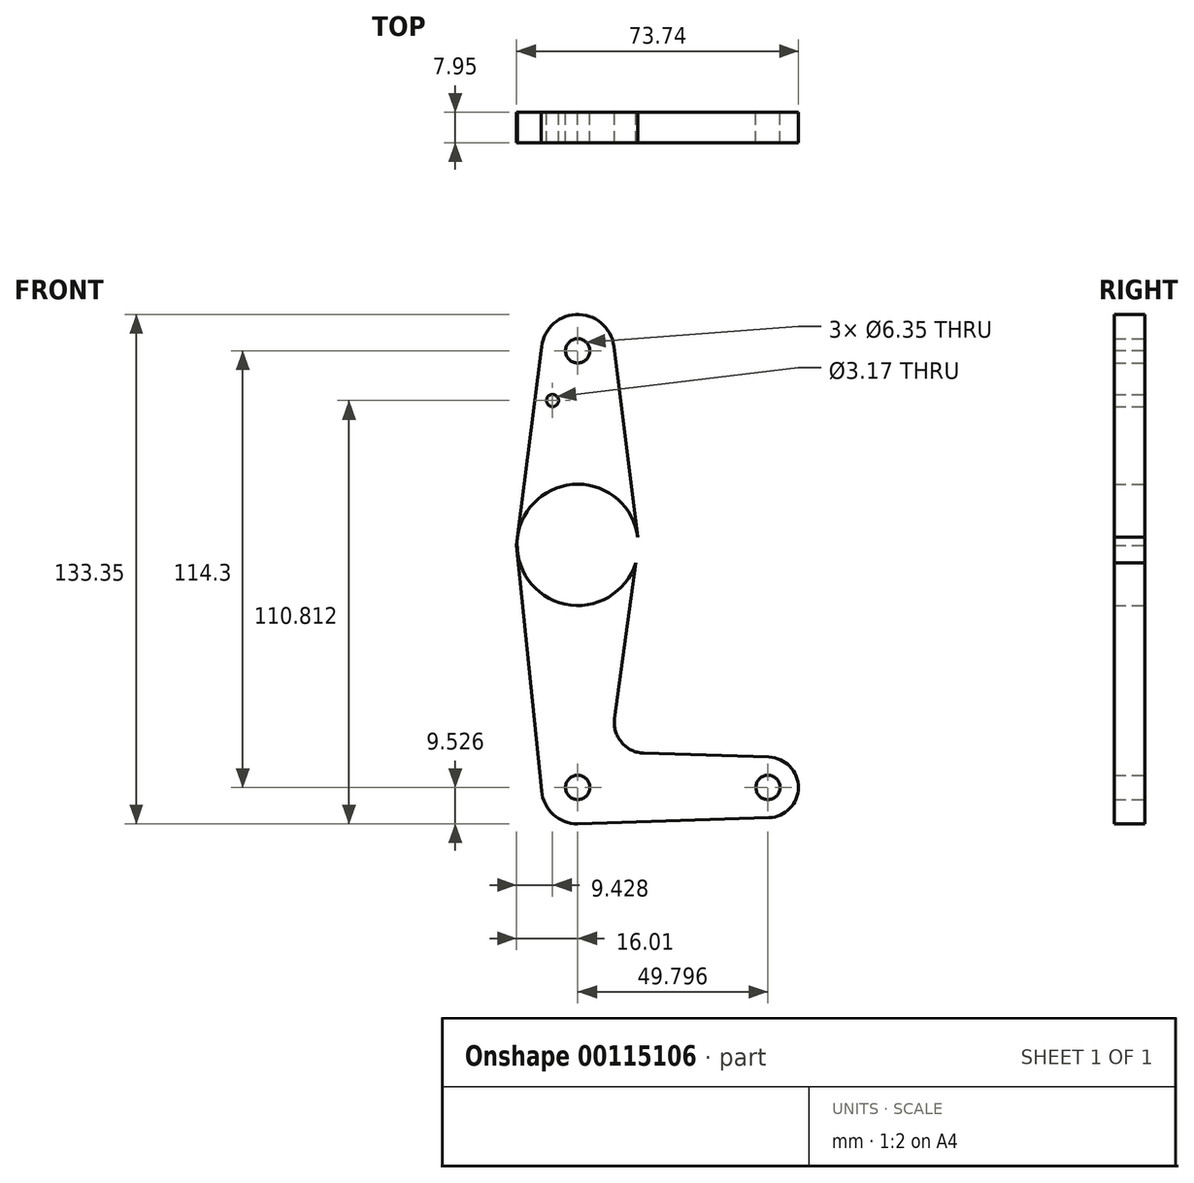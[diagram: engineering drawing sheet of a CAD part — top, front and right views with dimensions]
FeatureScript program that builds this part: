
annotation { "Feature Type Name" : "Feature", "Feature Type Description" : "" }
export const myFeature = defineFeature(function(context is Context, id is Id, definition is map)
    precondition{}
    {
        {
            var Q0;
            Q0=qCreatedBy(makeId("Front.planeOp"),FACE);
            var sketch = newSketch(context, id + "F0", { "sketchPlane" : qUnion([Q0])});
            skLineSegment(sketch, "E0", {"start": v(0, 46.97) * mm, "end": v(0, -67.33) * mm});
            skLineSegment(sketch, "E1", {"start": v(0, -67.33) * mm, "end": v(49.8, -67.33) * mm});
            skCircle(sketch, "E2", {"center": v(0, 46.97) * mm, "radius": 9.53 * mm});
            skCircle(sketch, "E3", {"center": v(0, -3.83) * mm, "radius": 15.88 * mm});
            skCircle(sketch, "E4", {"center": v(0, -67.33) * mm, "radius": 9.53 * mm});
            skCircle(sketch, "E5", {"center": v(49.8, -67.33) * mm, "radius": 7.94 * mm});
            skLineSegment(sketch, "E6", {"start": v(-9.52, 47.1) * mm, "end": v(-16.01, -3.92) * mm});
            skLineSegment(sketch, "E7", {"start": v(17.29, -58.36) * mm, "end": v(50.05, -59.4) * mm});
            skLineSegment(sketch, "E8", {"start": v(-16.01, -3.92) * mm, "end": v(-9.48, -68.3) * mm});
            skLineSegment(sketch, "E9", {"start": v(0, -76.86) * mm, "end": v(50.05, -75.27) * mm});
            skLineSegment(sketch, "E10", {"start": v(15.18, -8.49) * mm, "end": v(9.66, -49.35) * mm});
            skLineSegment(sketch, "E11", {"start": v(9.45, 48.16) * mm, "end": v(15.75, -1.85) * mm});
            skCircle(sketch, "E12", {"center": v(0, 46.97) * mm, "radius": 3.18 * mm});
            skCircle(sketch, "E13", {"center": v(0, -67.33) * mm, "radius": 3.18 * mm});
            skCircle(sketch, "E14", {"center": v(49.8, -67.33) * mm, "radius": 3.18 * mm});
            skCircle(sketch, "E15", {"center": v(0, 0) * mm, "radius": 3.18 * mm});
            skArc(sketch, "E16.filletArc", {"start": v(9.66, -49.35) * mm, "mid": v(11.47, -55.55) * mm, "end": v(17.29, -58.36) * mm});
            skCircle(sketch, "E17", {"center": v(-6.58, 33.95) * mm, "radius": 1.59 * mm});
            skSolve(sketch);
        }
        {
            var Q0;
            Q0=makeQuery(id+"F0.imprint","IMPRINT",FACE,{"disambiguationData":[TD([[makeQuery(id+"F0.imprint","IMPRINT",EDGE,{"derivedFrom":sQuery(id+"F0.wireOp",EDGE,"E17")}),-1.0]])]});
            var Q1;
            {var subQ5=sQuery(id+"F0.wireOp",EDGE,"E11");Q1=makeQuery(id+"F0.imprint","IMPRINT",FACE,{"disambiguationData":[TD([[makeQuery(id+"F0.imprint","IMPRINT",EDGE,{"derivedFrom":subQ5}),-1.0]])]});}
            var Q2;
            Q2=makeQuery(id+"F0.imprint","IMPRINT",FACE,{"disambiguationData":[TD([[makeQuery(id+"F0.imprint","IMPRINT",EDGE,{"derivedFrom":sQuery(id+"F0.wireOp",EDGE,"E12")}),-1.0]])]});
            var Q3;
            {var subQ0=sQuery(id+"F0.wireOp",EDGE,"E3");var subQ2=sQuery(id+"F0.wireOp",EDGE,"E0");var subQ3=makeQuery(id+"F0.imprint","INTERSECT",VERTEX,{"disambiguationData":[OD(0.0)],"derivedFrom":[subQ2,subQ0]});Q3=makeQuery(id+"F0.imprint","IMPRINT",FACE,{"disambiguationData":[TD([[makeQuery(id+"F0.imprint","IMPRINT",EDGE,{"disambiguationData":[TD([[subQ3,-1.0]])],"derivedFrom":subQ2}),1.0]])]});}
            var Q4;
            {var subQ0=sQuery(id+"F0.wireOp",EDGE,"E3");var subQ2=sQuery(id+"F0.wireOp",EDGE,"E0");var subQ4=makeQuery(id+"F0.imprint","INTERSECT",VERTEX,{"disambiguationData":[OD(0.0)],"derivedFrom":[subQ2,subQ0]});Q4=makeQuery(id+"F0.imprint","IMPRINT",FACE,{"disambiguationData":[TD([[makeQuery(id+"F0.imprint","IMPRINT",EDGE,{"disambiguationData":[TD([[subQ4,-1.0]])],"derivedFrom":subQ2}),-1.0]])]});}
            var Q5;
            {var subQ0=sQuery(id+"F0.wireOp",EDGE,"E8");Q5=makeQuery(id+"F0.imprint","IMPRINT",FACE,{"disambiguationData":[TD([[makeQuery(id+"F0.imprint","IMPRINT",EDGE,{"derivedFrom":subQ0}),1.0]])]});}
            var Q6;
            {var subQ10=sQuery(id+"F0.wireOp",EDGE,"E7");Q6=makeQuery(id+"F0.imprint","IMPRINT",FACE,{"disambiguationData":[TD([[makeQuery(id+"F0.imprint","IMPRINT",EDGE,{"derivedFrom":subQ10}),-1.0]])]});}
            var Q7;
            {var subQ0=sQuery(id+"F0.wireOp",EDGE,"E5");var subQ1=sQuery(id+"F0.wireOp",EDGE,"E1");var subQ2=makeQuery(id+"F0.imprint","INTERSECT",VERTEX,{"derivedFrom":[subQ1,subQ0]});Q7=makeQuery(id+"F0.imprint","IMPRINT",FACE,{"disambiguationData":[TD([[makeQuery(id+"F0.imprint","IMPRINT",EDGE,{"disambiguationData":[TD([[subQ2,1.0]])],"derivedFrom":subQ1}),-1.0]])]});}
            var Q8;
            {var subQ3=sQuery(id+"F0.wireOp",EDGE,"E4");var subQ8=sQuery(id+"F0.wireOp",EDGE,"E0");var subQ9=makeQuery(id+"F0.imprint","INTERSECT",VERTEX,{"derivedFrom":[subQ8,subQ3]});Q8=makeQuery(id+"F0.imprint","IMPRINT",FACE,{"disambiguationData":[TD([[makeQuery(id+"F0.imprint","IMPRINT",EDGE,{"disambiguationData":[TD([[subQ9,-1.0]])],"derivedFrom":subQ8}),-1.0]])]});}
            var Q9;
            {var subQ0=sQuery(id+"F0.wireOp",EDGE,"E4");var subQ1=sQuery(id+"F0.wireOp",EDGE,"E0");var subQ2=makeQuery(id+"F0.imprint","INTERSECT",VERTEX,{"derivedFrom":[subQ1,subQ0]});Q9=makeQuery(id+"F0.imprint","IMPRINT",FACE,{"disambiguationData":[TD([[makeQuery(id+"F0.imprint","IMPRINT",EDGE,{"disambiguationData":[TD([[subQ2,-1.0]])],"derivedFrom":subQ1}),1.0]])]});}
            var Q10;
            Q10=makeQuery(id+"F0.imprint","IMPRINT",FACE,{"disambiguationData":[TD([[makeQuery(id+"F0.imprint","IMPRINT",EDGE,{"derivedFrom":sQuery(id+"F0.wireOp",EDGE,"E14")}),-1.0]])]});
            extrude(context, id + "F1", {"entities" : qUnion([Q0, Q1, Q2, Q3, Q4, Q5, Q6, Q7, Q8, Q9, Q10]), "depth" : 7.95 * mm});
        }
    });
